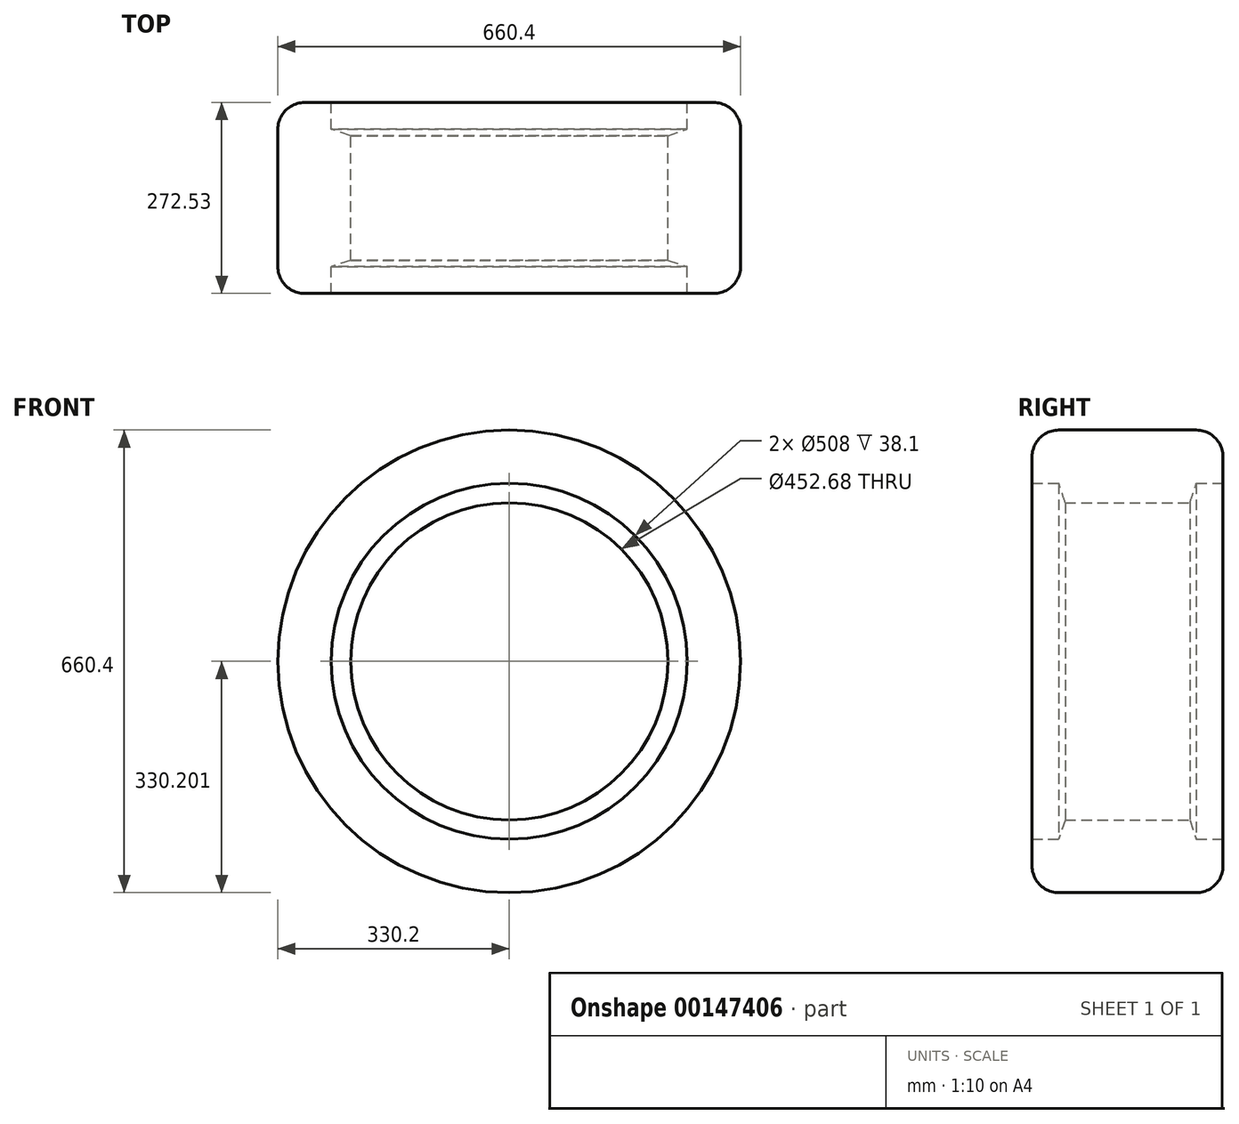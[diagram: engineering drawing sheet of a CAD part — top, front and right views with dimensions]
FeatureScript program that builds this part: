
annotation { "Feature Type Name" : "Feature", "Feature Type Description" : "" }
export const myFeature = defineFeature(function(context is Context, id is Id, definition is map)
    precondition{}
    {
        {
            var Q0;
            Q0=qCreatedBy(makeId("Right.planeOp"),FACE);
            var sketch = newSketch(context, id + "F0", { "sketchPlane" : qUnion([Q0])});
            skLineSegment(sketch, "E0.MirrorCS", {"start": v(-41.15, 425.6) * mm, "end": v(-3.05, 425.6) * mm});
            skLineSegment(sketch, "E1.MirrorCS", {"start": v(6.22, 397.93) * mm, "end": v(-3.05, 425.6) * mm});
            skLineSegment(sketch, "E2.MirrorCS", {"start": v(6.22, 397.93) * mm, "end": v(184.02, 397.93) * mm});
            skLineSegment(sketch, "E3.MirrorCS", {"start": v(184.02, 397.93) * mm, "end": v(193.28, 425.6) * mm});
            skLineSegment(sketch, "E4.MirrorCS", {"start": v(231.38, 425.6) * mm, "end": v(193.28, 425.6) * mm});
            skLineSegment(sketch, "E5", {"start": v(95.12, 171.6) * mm, "end": v(-601.05, 171.6) * mm});
            skPoint(sketch, "E5.endSnap0", {"position": v(95.12, 171.6) * mm});
            skLineSegment(sketch, "E6", {"start": v(-41.15, 425.6) * mm, "end": v(-41.15, 476.4) * mm});
            skLineSegment(sketch, "E7", {"start": v(231.38, 425.6) * mm, "end": v(231.38, 476.4) * mm});
            skLineSegment(sketch, "E8", {"start": v(-41.15, 476.4) * mm, "end": v(-41.15, 501.8) * mm});
            skLineSegment(sketch, "E9", {"start": v(-41.15, 501.8) * mm, "end": v(231.38, 501.8) * mm});
            skLineSegment(sketch, "E10", {"start": v(231.38, 476.4) * mm, "end": v(231.38, 501.8) * mm});
            skSolve(sketch);
        }
        {
            var Q0;
            Q0=makeQuery(id+"F0.imprint","IMPRINT",FACE,{"disambiguationData":[TD([[makeQuery(id+"F0.imprint","IMPRINT",EDGE,{"derivedFrom":sQuery(id+"F0.wireOp",EDGE,"E0.MirrorCS")}),1.0]])]});
            var Q1;
            Q1=sQuery(id+"F0.wireOp",EDGE,"E5");
            revolve(context, id + "F1", {"entities" : qUnion([Q0]), "axis" : qUnion([Q1]), "revolveType" : RevolveType.FULL});
        }
        {
            var Q0;
            Q0=makeQuery(id+"F1.opRevolve","SWEPT_EDGE",EDGE,{"disambiguationData":[OSD([sQuery(id+"F0.wireOp",EDGE,"E8"),sQuery(id+"F0.wireOp",EDGE,"E9")])]});
            var Q1;
            Q1=makeQuery(id+"F1.opRevolve","SWEPT_EDGE",EDGE,{"disambiguationData":[OSD([sQuery(id+"F0.wireOp",EDGE,"E9"),sQuery(id+"F0.wireOp",EDGE,"E10")])]});
            fillet(context, id + "F2", {"entities" : qUnion([Q0, Q1]), "radius" : 38.1 * mm, "tangentPropagation" : true, "allowEdgeOverflow" : false});
        }
    });
